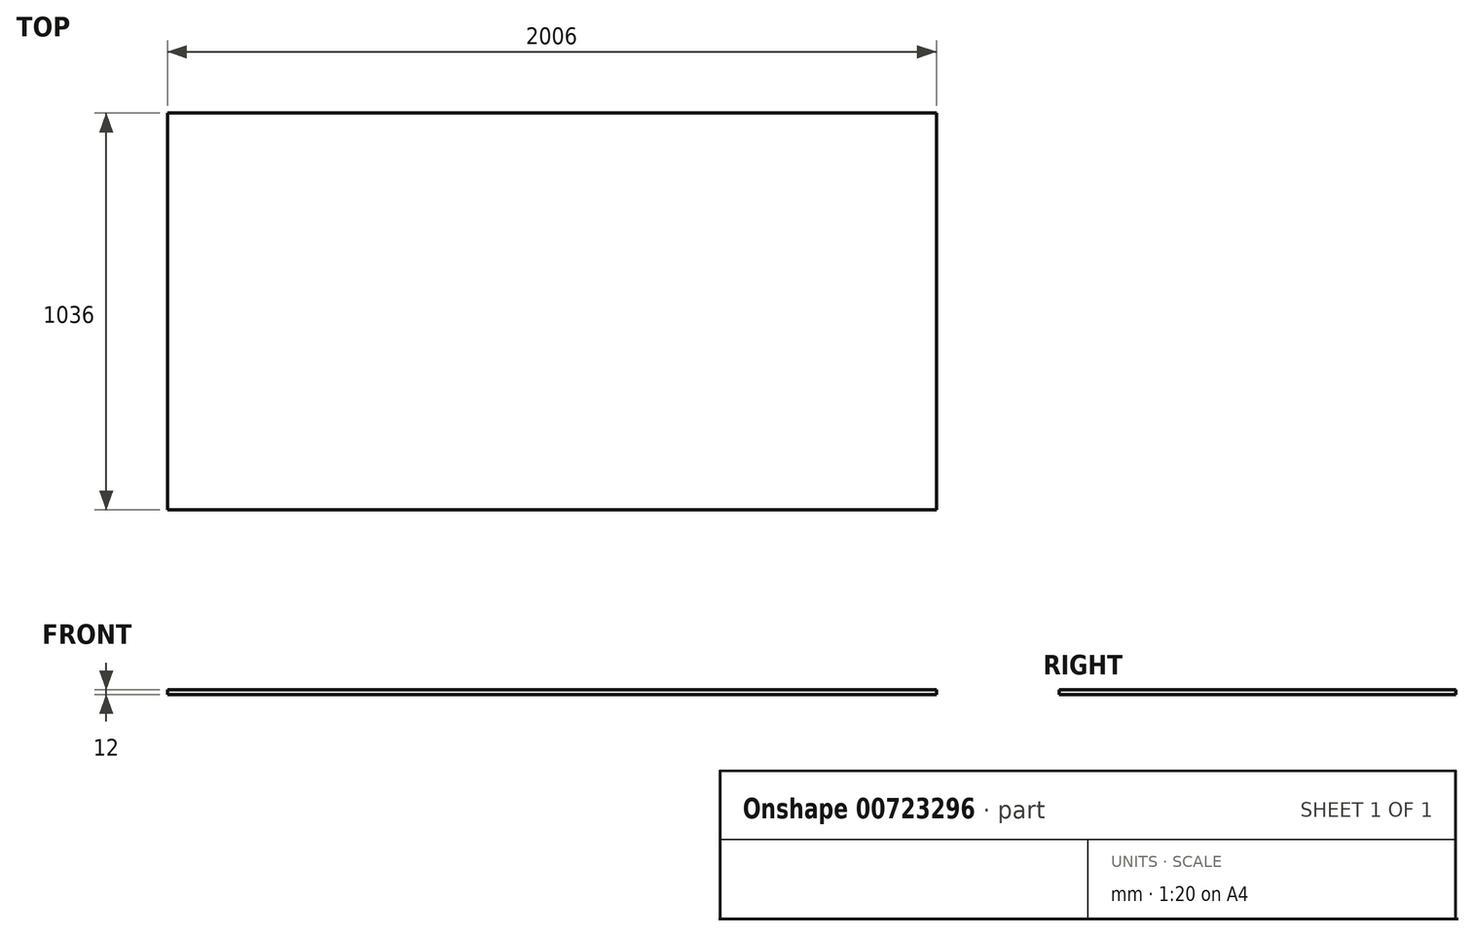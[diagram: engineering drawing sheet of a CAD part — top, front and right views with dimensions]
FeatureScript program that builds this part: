
annotation { "Feature Type Name" : "Feature", "Feature Type Description" : "" }
export const myFeature = defineFeature(function(context is Context, id is Id, definition is map)
    precondition{}
    {
        {
            var Q0;
            Q0=qCreatedBy(makeId("Top.planeOp"),FACE);
            var sketch = newSketch(context, id + "F0", { "sketchPlane" : qUnion([Q0])});
            skLineSegment(sketch, "E0.bottom", {"start": v(-1010.46, 639.64) * mm, "end": v(995.54, 639.64) * mm});
            skLineSegment(sketch, "E0.top", {"start": v(-1010.46, -396.36) * mm, "end": v(995.54, -396.36) * mm});
            skLineSegment(sketch, "E0.left", {"start": v(-1010.46, 639.64) * mm, "end": v(-1010.46, -396.36) * mm});
            skLineSegment(sketch, "E0.right", {"start": v(995.54, 639.64) * mm, "end": v(995.54, -396.36) * mm});
            skSolve(sketch);
        }
        {
            var Q0;
            Q0=makeQuery(id+"F0.imprint","IMPRINT",FACE,{"disambiguationData":[TD([[makeQuery(id+"F0.imprint","IMPRINT",EDGE,{"derivedFrom":sQuery(id+"F0.wireOp",EDGE,"E0.bottom")}),-1.0]])]});
            extrude(context, id + "F1", {"entities" : qUnion([Q0]), "depth" : 12 * mm, "offsetDistance" : 25 * mm});
        }
    });
